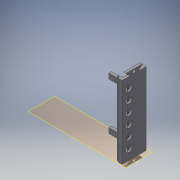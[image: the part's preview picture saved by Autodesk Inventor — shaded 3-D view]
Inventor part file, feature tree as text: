
AUTODESK INVENTOR PART (.ipt)
format: ipt  version: 2016 SP2 (Build 200236200, 236)  size: 287,232 bytes
history: native  units: mm
features: reference x14, extrude x8, sketch x8, chamfer x2, plane x1
ambient origin geometry x8: Origin, YZ Plane, XZ Plane, XY Plane, X Axis, Y Axis, Z Axis, Center Point
bodies: Volumenkörper1 (feature_tree)
feature tree (33):
  plane  "Arbeitsebene1"
  extrude  "Extrusion1"  Depth=0.6mm
  extrude  "Extrusion2"  Depth=15.0mm
  extrude  "Extrusion3"  Depth=4.5mm
  extrude  "Extrusion4"  TaperAngle=45.0deg  [1 undecoded]
  chamfer  "Fase1"  Distance=0.8mm
  extrude  "Extrusion5"  Depth=1.0mm
  extrude  "Extrusion6"  Depth=1.0mm
  chamfer  "Fase2"  Distance=0.8mm
  extrude  "Extrusion7"  Depth=1.0mm
  extrude  "Extrusion8"  Depth=2.0mm
  sketch  "Skizze1"  dims[d0=0.6mm d2=6.1mm]
  reference  "Referenz1"
  reference  "Referenz2"
  reference  "Referenz3"
  reference  "Referenz4"
  reference  "Referenz5"
  reference  "Referenz6"
  reference  "Referenz7"
  reference  "Referenz8"
  reference  "Referenz9"
  reference  "Referenz10"
  reference  "Referenz11"
  sketch  "Skizze2"  dims[d4=12.0mm d5=15.0mm]
  reference  "Referenz12"
  sketch  "Skizze3"  dims[d6=1.6mm d7=4.5mm]
  sketch  "Skizze4"  dims[d8=18.0mm d9=45.0deg]
  reference  "Referenz13"
  reference  "Referenz14"
  sketch  "Skizze5"  dims[d10=1.026067mm]
  sketch  "Skizze7"  dims[d11=6.0mm]
  sketch  "Skizze8"  dims[d12=1.0mm]
  sketch  "Skizze9"  dims[d13=0.8mm d14=0.8mm d15=1.0mm d16=1.0mm d17=0.8mm d18=1.0mm d19=2.0mm d20=138.8mm d21=0.0mm d22=4.4mm d23=0.0mm d24=6.0mm d25=6.0mm d26=3.5mm d27=0.0mm d28=32.65mm d29=0.0mm d30=2.5mm d31=2.0mm d32=45.0deg d33=3.5mm d34=3.5mm d35=5.0mm d36=5.0mm d37=5.0mm d38=5.0mm d39=36.75mm d40=0.0mm d41=5.8mm d43=5.8mm d44=2.5mm d45=0.0mm d46=2.0mm d47=2.0mm d48=45.0deg d49=15.0mm d50=19.4mm d51=60.0mm d53=20.0mm d54=10.0mm d56=10.0mm d58=19.4mm d59=3.9mm d60=0.0mm d61=12.0mm d62=12.0mm d63=12.0mm d64=12.0mm d65=12.0mm d66=12.0mm d67=3.9mm d68=0.0mm d69=3.9mm]
note: 1 required parameter value undecoded (feature->parameter linkage not recoverable at this tier; creation-order binding heuristic only, values carry confidence <= 0.55)
